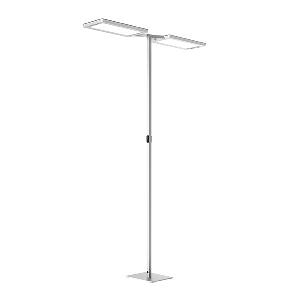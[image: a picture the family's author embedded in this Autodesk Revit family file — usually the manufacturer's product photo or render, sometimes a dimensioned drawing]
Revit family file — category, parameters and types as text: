
# Revit family: yara_doublet_-_yts_2_15000_vtl_rx_sr_cee_s0_c_114268000-00808496_f4a1
name_source: partatom
category: Lighting Fixtures
units: mm (PartAtom-declared; Revit-internal decimal feet)

## family parameters
Cut with Voids When Loaded = No
Host = Face
Light Source = No
Part Type = Normal
Room Calculation Point = No
Round Connector Dimension = Use Diameter
Shared = No

## types (1)
- YARA.doubleT - YTS 2/15000/VTL/RX/SR/CEE/S0/C (1 x LED, 15000 lm, VTL)
    Apparent Load = 214 VA
    Approval mark = CE
    CIE Flux Codes = 58 87 97 13 100
    Color Rendering = 80-89
    Color Temperature = VTL
    Control Gear = Electronic ballast
    Default Elevation = 1800 mm
    Description = YTS 2/15000/VTL/RX/SR/CEE/S0/R|Free-standing luminaire|light source: LED|work equipment: Electronic ballast DALI|connected load: 220-240 V, 50/60 Hz|Power consumption: approx. 210 W|power factor: approx. 0,966|luminous flux: 30000 lm|luminous efficacy: 142 lm/W|light distribution: Direct/indirect|direct ratio: approx. 13 %|colour temperature: Daylight, ca. 2700-6500 K|color rendering index (CRI): >= 80|chromaticity tolerance:  3 SDCM|technology: Multiple daylight-dependent motion sensors|operation: Wireless switch|luminaire body|material: Aluminium/plastic|surface: Powder coatet|colour: Silver metallic|lamp cover: Acrylic (PMMA), Satine, Structured|tubular section|material: Steel tube|surface: Powder-coated|Form: Tubular section upright|colour of tubular section: Silver metallic|luminaire base|Form: Rectangular flat|weight (net): approx. 24.0 kg|mains lead: 3.00 m Mains plug CEE 7/VII|Fastening: Floor standing base|glare control: Conical prismatic screen|luminance(L65): <= 2700 cd/m|unified glare rating(4H 8H): <=  16|special features: App control, Asymmetric radiation, Biodynamic light VTL, Direct and indirect lighting component with edge light and light guidetechnology for a homogeneous light exit, Flicker-free, LTX multisensor for workplace optimisation, Magnetic control panel, freely positionable, Optional LTX Cloud connection, TALK Bluetooth|Approval mark: VDE - ENEC|
    Frequency = 50 Hz, 60 Hz
    Height = 24 mm  [stored 0.0787402 ft]
    Lamp = 1 x LED
    Lamp Light Flux = 15000 lm
    Lamp count = 1
    Length = 690 mm
    Luminous efficacy = 140 lm/W
    Manufacturer = Waldmann
    ModVariant = No
    Model = 114268000-00808496
    Mounting Place = Floor
    Mounting Type = Freestanding
    Number of Poles = 1
    OnlyDefault = Yes
    Power Factor = 1
    Product Name = YARA.doubleT - YTS 2/15000/VTL/RX/SR/CEE/S0/C
    Product group = Free standing luminaire
    ProductGroupID = 13
    Protection Class = Protection class I
    Protection Degree = IP 20
    RLX_Detail_Level = 1
    RlxData = <blob elided: 63793 chars, md5=b64b48d5>
    Socket = socket
    Standby Power = 0 W
    System Light Flux = 30000 lm
    System Power = 214 W
    Type Comments = Product without accessories
    Type Image = yts-rx-sr-r.jpg
    URL = http://relux.com
    VarID = ---
    Voltage = 230 V
    Voltage Range = 220-240 V
    Weight = 0.00 kg
    Width = 358 mm

note: [stored X ft] marks values corroborated as IEEE doubles in the binary element streams (Revit-internal decimal feet)

## geometry (parser evidence)
native form markers: Blend x4, Sweep x18
no freeform markers — native parametric forms only
